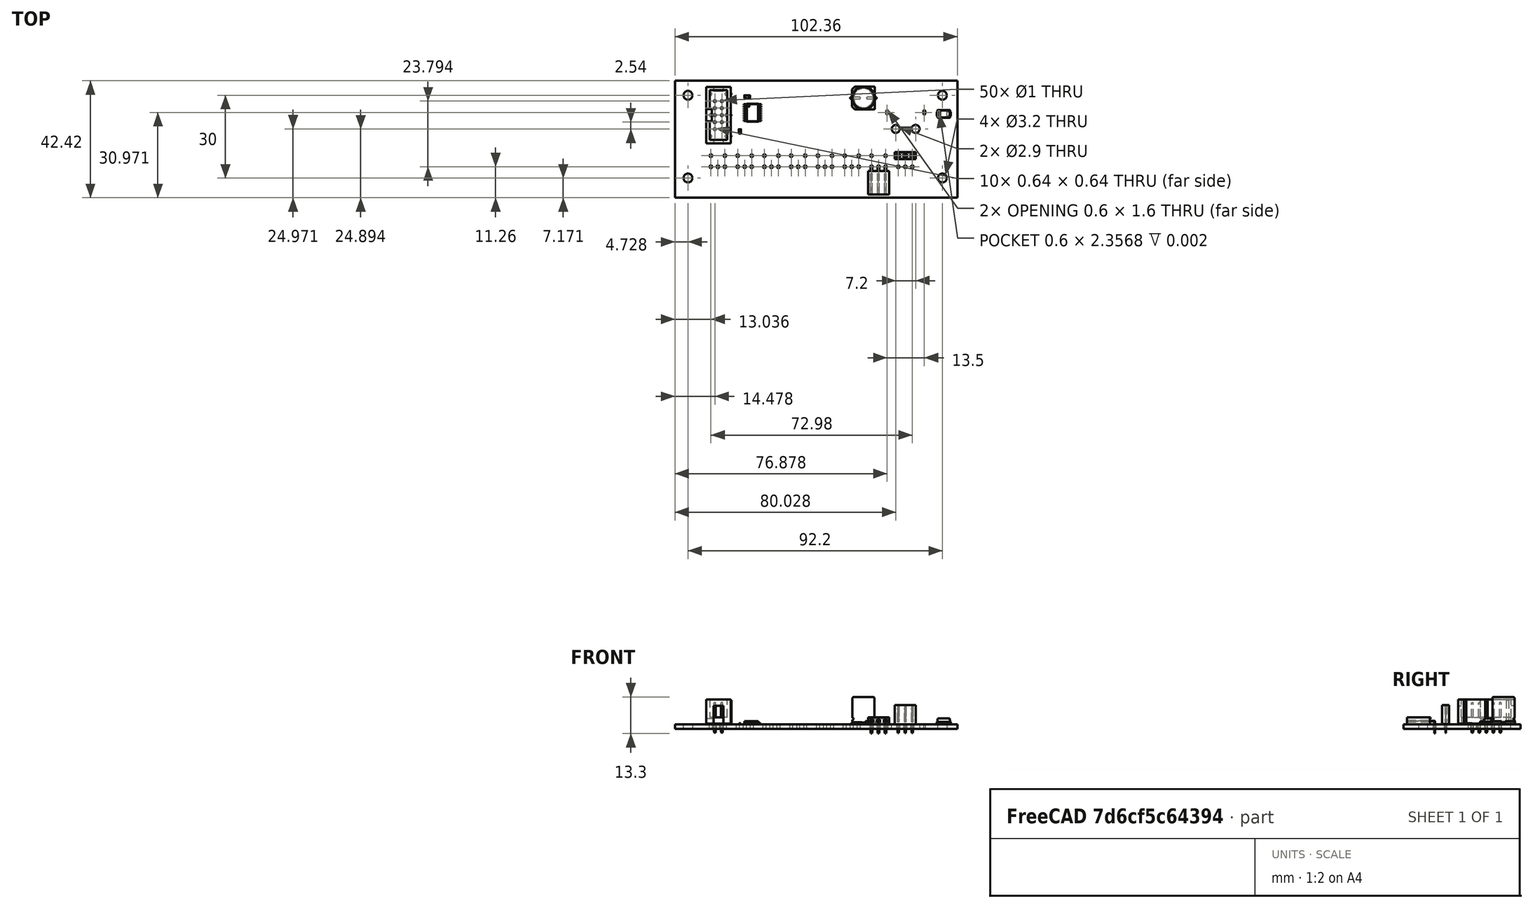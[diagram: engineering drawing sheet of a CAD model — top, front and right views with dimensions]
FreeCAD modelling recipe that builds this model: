
FCSTD DOCUMENT  (FreeCAD 1.0R39109 (Git))
Label: LED Board1
License: All rights reserved
LicenseURL: http://en.wikipedia.org/wiki/All_rights_reserved
objects: App::Link×23, Part::Feature×9, App::Part×4, PartDesign::CoordinateSystem×1, Sketcher::SketchObject×1
note: 12 computed .brp shape members not serialized (recipe doc carries the construction recipe); baked Part::Feature solids carry a one-line shape summary decoded from their .brp

FEATURE [PartDesign::CoordinateSystem] Local_CS_4b10
  AttacherType = Attacher::AttachEngine3D
  MapMode = 2
FEATURE [Part::Feature] Pcb_4b10
  Placement = pos=(-68.072,39.751,0) rot=(0,0,1;0rad)
  shape: bbox 102.4 x 42.42 x 1.6 mm, 74 faces (baked)
FEATURE [Sketcher::SketchObject] PCB_Sketch_4b10
  ArcFitTolerance = 1e-06
  FullyConstrained = false
  MakeInternals = false
  sketch-geometry (4):
    g0: LineSegment StartX=0 StartY=0 StartZ=0 EndX=102.362 EndY=0 EndZ=0
    g1: LineSegment StartX=102.362 StartY=0 StartZ=0 EndX=102.362 EndY=-42.418 EndZ=0
    g2: LineSegment StartX=102.362 StartY=-42.418 StartZ=0 EndX=0 EndY=-42.418 EndZ=0
    g3: LineSegment StartX=0 StartY=-42.418 StartZ=0 EndX=0 EndY=0 EndZ=0
  constraints (4):
    c: Coincident(g2,g3)
    c: Coincident(g0,g3)
    c: Coincident(g1,g2)
    c: Coincident(g0,g1)
FEATURE [App::Part] Board_Geoms_4b10
  Group = -> [Pcb_4b10,PCB_Sketch_4b10]
  Origin = -> Origin
FEATURE [Part::Feature] Shape  label="R2_R_0603_1608Metric_c5dc6eb5ae7c"
  Placement = pos=(23.528,-18.379,0) rot=(0,0,-1;1.5708rad)
  shape: bbox 0.8 x 1.6 x 0.45 mm, 26 faces (baked)
FEATURE [Part::Feature] Shape001  label="J7_PinSocket_1x03_P254mm_Horizontal_d9de771da954"
  Placement = pos=(71.236,-31.16,0) rot=(0,0,1;1.5708rad)
  shape: bbox 7.62 x 10.13 x 5.84 mm, 115 faces (baked)
FEATURE [Part::Feature] Shape002  label="J16_PinSocket_1x03_P254mm_Vertical_fb3ea0eaffca"
  Placement = pos=(80.936,-27.153,0) rot=(0,0,1;1.5708rad)
  shape: bbox 7.62 x 2.54 x 10.1 mm, 103 faces (baked)
FEATURE [App::Link] J16_PinSocket_1x03_P254mm_Vertical_fb3ea0eaffca_ln_  label="J13_PinSocket_1x03_P254mm_Vertical_f3c5acdf76a0"
  LinkPlacement = pos=(51.836,-27.153,0) rot=(0,0,1;1.5708rad)
  LinkedObject = -> Shape002
  Placement = pos=(51.836,-27.153,0) rot=(0,0,1;1.5708rad)
FEATURE [App::Link] J7_PinSocket_1x03_P254mm_Horizontal_d9de771da954_ln_  label="J6_PinSocket_1x03_P254mm_Horizontal_25e45af0490d"
  LinkPlacement = pos=(61.536,-31.16,0) rot=(0,0,1;1.5708rad)
  LinkedObject = -> Shape001
  Placement = pos=(61.536,-31.16,0) rot=(0,0,1;1.5708rad)
FEATURE [App::Link] J16_PinSocket_1x03_P254mm_Vertical_fb3ea0eaffca_ln_001  label="J14_PinSocket_1x03_P254mm_Vertical_e2216f14c2a5"
  LinkPlacement = pos=(61.536,-27.153,0) rot=(0,0,1;1.5708rad)
  LinkedObject = -> Shape002
  Placement = pos=(61.536,-27.153,0) rot=(0,0,1;1.5708rad)
FEATURE [App::Link] J7_PinSocket_1x03_P254mm_Horizontal_d9de771da954_ln_001  label="J4_PinSocket_1x03_P254mm_Horizontal_87e6043b4534"
  LinkPlacement = pos=(42.136,-31.16,0) rot=(0,0,1;1.5708rad)
  LinkedObject = -> Shape001
  Placement = pos=(42.136,-31.16,0) rot=(0,0,1;1.5708rad)
FEATURE [App::Link] J16_PinSocket_1x03_P254mm_Vertical_fb3ea0eaffca_ln_002  label="J10_PinSocket_1x03_P254mm_Vertical_f2cf4f472ca2"
  LinkPlacement = pos=(22.736,-27.153,0) rot=(0,0,1;1.5708rad)
  LinkedObject = -> Shape002
  Placement = pos=(22.736,-27.153,0) rot=(0,0,1;1.5708rad)
FEATURE [App::Link] R2_R_0603_1608Metric_c5dc6eb5ae7c_ln_  label="R7_R_0603_1608Metric_35a208321f07"
  LinkPlacement = pos=(31.4909,-18.379,0) rot=(0,0,-1;1.5708rad)
  LinkedObject = -> Shape
  Placement = pos=(31.4909,-18.379,0) rot=(0,0,-1;1.5708rad)
FEATURE [App::Link] J7_PinSocket_1x03_P254mm_Horizontal_d9de771da954_ln_002  label="J1_PinSocket_1x03_P254mm_Horizontal_575c6b300b27"
  LinkPlacement = pos=(13.036,-31.16,0) rot=(0,0,1;1.5708rad)
  LinkedObject = -> Shape001
  Placement = pos=(13.036,-31.16,0) rot=(0,0,1;1.5708rad)
FEATURE [App::Link] R2_R_0603_1608Metric_c5dc6eb5ae7c_ln_001  label="R9_R_0603_1608Metric_ae4a19d8cb1b"
  LinkPlacement = pos=(36.557,-13.5089,0) rot=(0,0,1;0rad)
  LinkedObject = -> Shape
  Placement = pos=(36.557,-13.5089,0) rot=(0,0,1;0rad)
FEATURE [App::Link] J16_PinSocket_1x03_P254mm_Vertical_fb3ea0eaffca_ln_003  label="J11_PinSocket_1x03_P254mm_Vertical_82d4afe2cb67"
  LinkPlacement = pos=(32.436,-27.153,0) rot=(0,0,1;1.5708rad)
  LinkedObject = -> Shape002
  Placement = pos=(32.436,-27.153,0) rot=(0,0,1;1.5708rad)
FEATURE [Part::Feature] Shape003  label="C1_C_0805_2012Metric_fcbd4ca8fac4"
  Placement = pos=(26.162,-5.842,0) rot=(0,0,1;0rad)
  shape: bbox 2 x 1.25 x 1.25 mm, 28 faces (baked)
FEATURE [App::Link] J7_PinSocket_1x03_P254mm_Horizontal_d9de771da954_ln_003  label="J5_PinSocket_1x03_P254mm_Horizontal_a0c3deebe20e"
  LinkPlacement = pos=(51.836,-31.16,0) rot=(0,0,1;1.5708rad)
  LinkedObject = -> Shape001
  Placement = pos=(51.836,-31.16,0) rot=(0,0,1;1.5708rad)
FEATURE [Part::Feature] Shape004  label="D1_D_SMA_93b1cf89d40d"
  Placement = pos=(97.428,-11.999,0) rot=(0,0,1;0rad)
  shape: bbox 5 x 2.7 x 2.22 mm, 41 faces (baked)
FEATURE [App::Link] R2_R_0603_1608Metric_c5dc6eb5ae7c_ln_002  label="R10_R_0603_1608Metric_f7528a99d7de"
  LinkPlacement = pos=(45.083,-13.249,0) rot=(0,0,1;0rad)
  LinkedObject = -> Shape
  Placement = pos=(45.083,-13.249,0) rot=(0,0,1;0rad)
FEATURE [App::Link] R2_R_0603_1608Metric_c5dc6eb5ae7c_ln_003  label="R3_R_0603_1608Metric_71b5a22a33ce"
  LinkPlacement = pos=(25.128,-18.379,0) rot=(0,0,-1;1.5708rad)
  LinkedObject = -> Shape
  Placement = pos=(25.128,-18.379,0) rot=(0,0,-1;1.5708rad)
FEATURE [App::Link] R2_R_0603_1608Metric_c5dc6eb5ae7c_ln_004  label="R5_R_0603_1608Metric_eeab90750359"
  LinkPlacement = pos=(28.328,-18.379,0) rot=(0,0,-1;1.5708rad)
  LinkedObject = -> Shape
  Placement = pos=(28.328,-18.379,0) rot=(0,0,-1;1.5708rad)
FEATURE [App::Link] R2_R_0603_1608Metric_c5dc6eb5ae7c_ln_005  label="R8_R_0603_1608Metric_7e36c6c63596"
  LinkPlacement = pos=(33.128,-18.379,0) rot=(0,0,-1;1.5708rad)
  LinkedObject = -> Shape
  Placement = pos=(33.128,-18.379,0) rot=(0,0,-1;1.5708rad)
FEATURE [App::Link] J7_PinSocket_1x03_P254mm_Horizontal_d9de771da954_ln_004  label="J2_PinSocket_1x03_P254mm_Horizontal_0ca650b14731"
  LinkPlacement = pos=(22.736,-31.16,0) rot=(0,0,1;1.5708rad)
  LinkedObject = -> Shape001
  Placement = pos=(22.736,-31.16,0) rot=(0,0,1;1.5708rad)
FEATURE [Part::Feature] Shape005  label="C2_CP_Elec_8x10_957ff0fd7096"
  Placement = pos=(68.328,-6.249,0) rot=(0,0,1;0rad)
  shape: bbox 10.73 x 10.92 x 10 mm, 41 faces (baked)
FEATURE [App::Link] J16_PinSocket_1x03_P254mm_Vertical_fb3ea0eaffca_ln_004  label="J12_PinSocket_1x03_P254mm_Vertical_4e3a082270ae"
  LinkPlacement = pos=(42.136,-27.153,0) rot=(0,0,1;1.5708rad)
  LinkedObject = -> Shape002
  Placement = pos=(42.136,-27.153,0) rot=(0,0,1;1.5708rad)
FEATURE [App::Link] J16_PinSocket_1x03_P254mm_Vertical_fb3ea0eaffca_ln_005  label="J9_PinSocket_1x03_P254mm_Vertical_034de2e4f99c"
  LinkPlacement = pos=(13.036,-27.153,0) rot=(0,0,1;1.5708rad)
  LinkedObject = -> Shape002
  Placement = pos=(13.036,-27.153,0) rot=(0,0,1;1.5708rad)
FEATURE [App::Link] R2_R_0603_1608Metric_c5dc6eb5ae7c_ln_006  label="R4_R_0603_1608Metric_25bf5737a32f"
  LinkPlacement = pos=(26.728,-18.379,0) rot=(0,0,-1;1.5708rad)
  LinkedObject = -> Shape
  Placement = pos=(26.728,-18.379,0) rot=(0,0,-1;1.5708rad)
FEATURE [App::Link] J16_PinSocket_1x03_P254mm_Vertical_fb3ea0eaffca_ln_006  label="J15_PinSocket_1x03_P254mm_Vertical_1073ababdb63"
  LinkPlacement = pos=(71.236,-27.153,0) rot=(0,0,1;1.5708rad)
  LinkedObject = -> Shape002
  Placement = pos=(71.236,-27.153,0) rot=(0,0,1;1.5708rad)
FEATURE [App::Link] J7_PinSocket_1x03_P254mm_Horizontal_d9de771da954_ln_005  label="J3_PinSocket_1x03_P254mm_Horizontal_0d159cc4f01e"
  LinkPlacement = pos=(32.436,-31.16,0) rot=(0,0,1;1.5708rad)
  LinkedObject = -> Shape001
  Placement = pos=(32.436,-31.16,0) rot=(0,0,1;1.5708rad)
FEATURE [App::Link] R2_R_0603_1608Metric_c5dc6eb5ae7c_ln_007  label="R6_R_0603_1608Metric_f26ad001bf2c"
  LinkPlacement = pos=(29.928,-18.379,0) rot=(0,0,-1;1.5708rad)
  LinkedObject = -> Shape
  Placement = pos=(29.928,-18.379,0) rot=(0,0,-1;1.5708rad)
FEATURE [Part::Feature] Shape006  label="J18_IDC_Header_2x05_P254mm_Vertical_4ae456b9b855"
  Placement = pos=(14.478,-7.366,0) rot=(0,0,1;0rad)
  shape: bbox 9.1 x 20.36 x 12.1 mm, 222 faces (baked)
FEATURE [App::Link] R2_R_0603_1608Metric_c5dc6eb5ae7c_ln_008  label="R1_R_0603_1608Metric_185892be60db"
  LinkPlacement = pos=(21.928,-18.379,0) rot=(0,0,-1;1.5708rad)
  LinkedObject = -> Shape
  Placement = pos=(21.928,-18.379,0) rot=(0,0,-1;1.5708rad)
FEATURE [Part::Feature] Shape007  label="U1_TSSOP_20_44x65mm_P065mm_d0ceabb486c1"
  Placement = pos=(28.1255,-11.553,0) rot=(0,0,1;0rad)
  shape: bbox 6.4 x 6.5 x 1.2 mm, 336 faces (baked)
FEATURE [App::Link] J7_PinSocket_1x03_P254mm_Horizontal_d9de771da954_ln_006  label="J8_PinSocket_1x03_P254mm_Horizontal_741a1f20863a"
  LinkPlacement = pos=(80.936,-31.16,0) rot=(0,0,1;1.5708rad)
  LinkedObject = -> Shape001
  Placement = pos=(80.936,-31.16,0) rot=(0,0,1;1.5708rad)
FEATURE [App::Part] Top_4b10
  Group = -> [Shape,Shape001,Shape002,J16_PinSocket_1x03_P254mm_Vertical_fb3ea0eaffca_ln_,J7_PinSocket_1x03_P254mm_Horizontal_d9de771da954_ln_,J16_PinSocket_1x03_P254mm_Vertical_fb3ea0eaffca_ln_001,J7_PinSocket_1x03_P254mm_Horizontal_d9de771da954_ln_001,J16_PinSocket_1x03_P254mm_Vertical_fb3ea0eaffca_ln_002,R2_R_0603_1608Metric_c5dc6eb5ae7c_ln_,J7_PinSocket_1x03_P254mm_Horizontal_d9de771da954_ln_002,+21 more]
  Origin = -> Origin003
FEATURE [App::Part] Step_Models_4b10
  Group = -> [Top_4b10]
  Origin = -> Origin002
FEATURE [App::Part] Board_4b10  label="LED Board"
  Group = -> [Local_CS_4b10,Board_Geoms_4b10,Step_Models_4b10]
  Origin = -> Origin001
